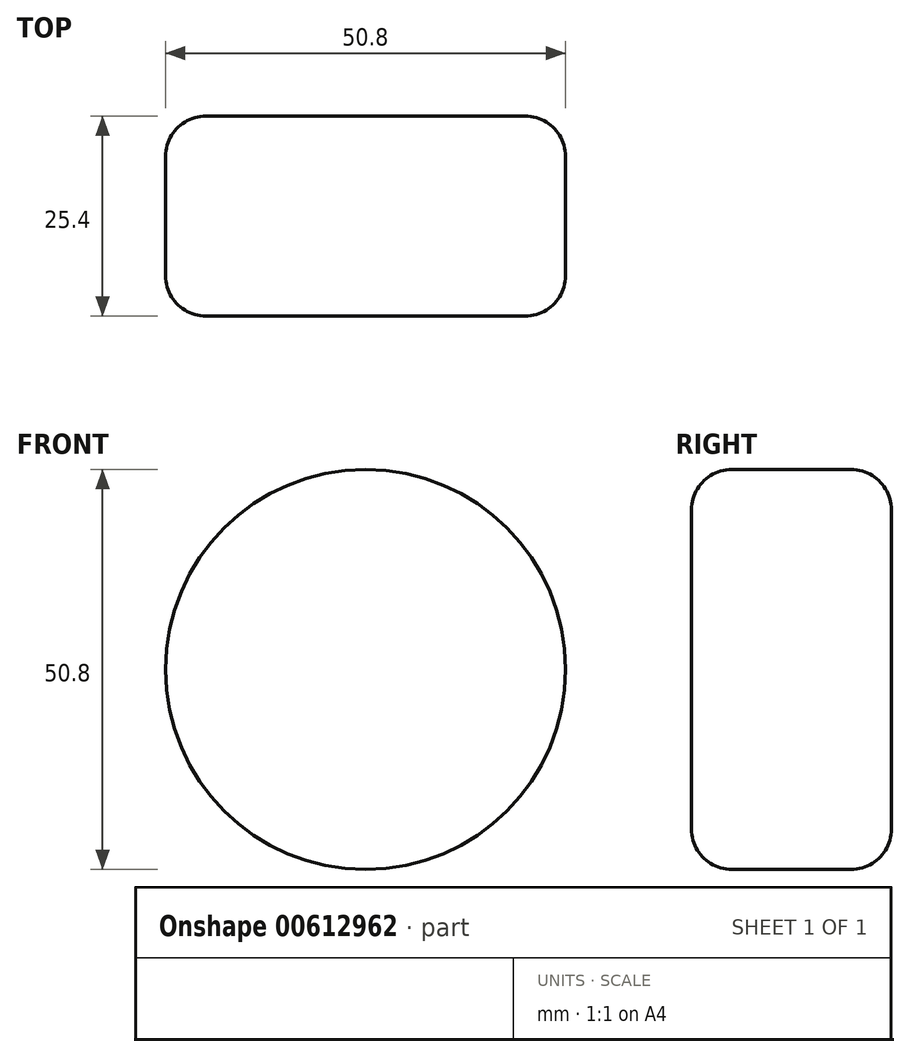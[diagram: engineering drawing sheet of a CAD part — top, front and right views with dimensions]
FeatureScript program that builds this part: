
annotation { "Feature Type Name" : "Feature", "Feature Type Description" : "" }
export const myFeature = defineFeature(function(context is Context, id is Id, definition is map)
    precondition{}
    {
        {
            var Q0;
            Q0=qCreatedBy(makeId("Front.planeOp"),FACE);
            var sketch = newSketch(context, id + "F0", { "sketchPlane" : qUnion([Q0])});
            skCircle(sketch, "E0", {"center": v(0, 0) * mm, "radius": 25.4 * mm});
            skSolve(sketch);
        }
        {
            var Q0;
            Q0=makeQuery(id+"F0.imprint","IMPRINT",FACE,{"disambiguationData":[TD([[makeQuery(id+"F0.imprint","IMPRINT",EDGE,{"derivedFrom":sQuery(id+"F0.wireOp",EDGE,"E0")}),1.0]])]});
            extrude(context, id + "F1", {"entities" : qUnion([Q0]), "endBound" : BoundingType.SYMMETRIC, "depth" : 25.4 * mm, "offsetDistance" : 25.4 * mm});
        }
        {
            var Q0;
            Q0=makeQuery(id+"F1.opExtrude","CAP_EDGE",EDGE,{"disambiguationData":[OSD([sQuery(id+"F0.wireOp",EDGE,"E0")])],"isStart":false});
            var Q1;
            Q1=makeQuery(id+"F1.opExtrude","CAP_EDGE",EDGE,{"disambiguationData":[OSD([sQuery(id+"F0.wireOp",EDGE,"E0")])],"isStart":true});
            fillet(context, id + "F2", {"entities" : qUnion([Q0, Q1]), "radius" : 5.08 * mm, "tangentPropagation" : true, "allowEdgeOverflow" : false});
        }
    });
